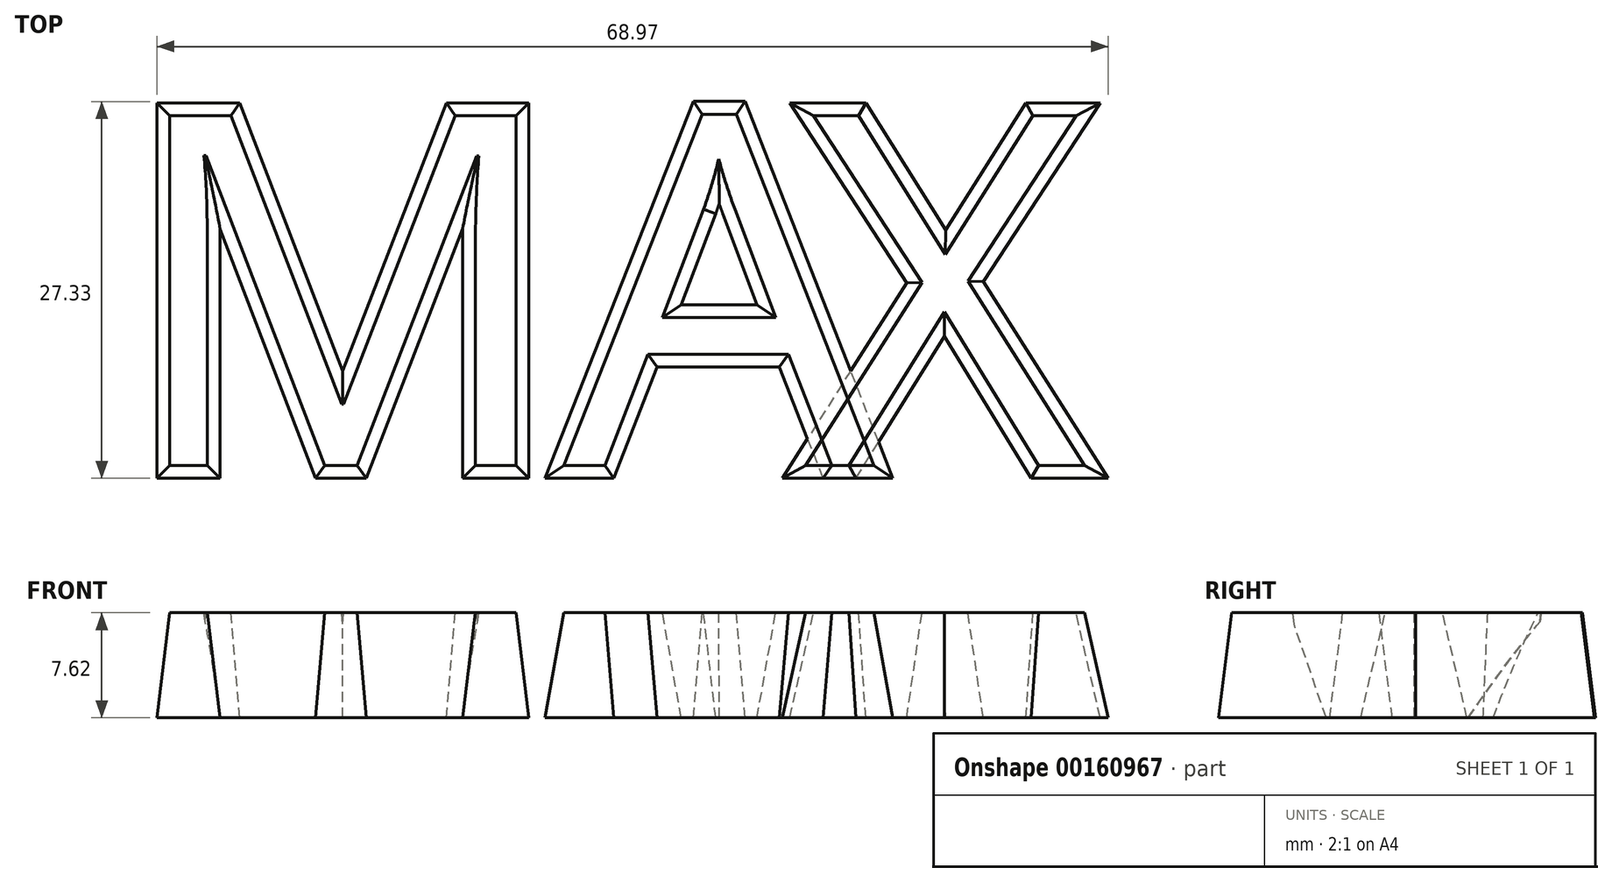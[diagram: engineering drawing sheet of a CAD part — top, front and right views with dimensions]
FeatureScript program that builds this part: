
annotation { "Feature Type Name" : "Feature", "Feature Type Description" : "" }
export const myFeature = defineFeature(function(context is Context, id is Id, definition is map)
    precondition{}
    {
        {
            var Q0;
            Q0=qCreatedBy(makeId("Top.planeOp"),FACE);
            var sketch = newSketch(context, id + "F0", { "sketchPlane" : qUnion([Q0])});
            skText(sketch, "E0", { "text": "MAX", "fontName": "OpenSans-Regular.ttf"});
            const initialGuessF0  = {"E0": [0.00322, 0, 1, 0, 0.02557]};
            skSetInitialGuess(sketch, initialGuessF0);
            skSolve(sketch);
        }
        {
            var Q0;
            Q0 = qSketchRegion(id + "F0", true);
            extrude(context, id + "F1", {"entities" : qUnion([Q0]), "oppositeDirection" : true, "depth" : 7.62 * mm, "hasDraft" : true, "draftAngle" : 7 * degree});
        }
        {
            var Q0;
            Q0=makeQuery(id+"F1.opExtrude","SWEPT_BODY",BODY,{"disambiguationData":[OSD([sQuery(id+"F0.wireOp",EDGE,"E0.sketch_text.stroke-31"),sQuery(id+"F0.wireOp",EDGE,"E0.sketch_text.stroke-32"),sQuery(id+"F0.wireOp",EDGE,"E0.sketch_text.stroke-33"),sQuery(id+"F0.wireOp",EDGE,"E0.sketch_text.stroke-34"),sQuery(id+"F0.wireOp",EDGE,"E0.sketch_text.stroke-35"),sQuery(id+"F0.wireOp",EDGE,"E0.sketch_text.stroke-36"),sQuery(id+"F0.wireOp",EDGE,"E0.sketch_text.stroke-37"),sQuery(id+"F0.wireOp",EDGE,"E0.sketch_text.stroke-38"),sQuery(id+"F0.wireOp",EDGE,"E0.sketch_text.stroke-39"),sQuery(id+"F0.wireOp",EDGE,"E0.sketch_text.stroke-40"),sQuery(id+"F0.wireOp",EDGE,"E0.sketch_text.stroke-41"),sQuery(id+"F0.wireOp",EDGE,"E0.sketch_text.stroke-42")])]});
            var Q1;
            Q1=makeQuery(id+"F1.opExtrude","CAP_EDGE",EDGE,{"disambiguationData":[OSD([sQuery(id+"F0.wireOp",EDGE,"E0.sketch_text.stroke-21")])],"isStart":false});
            transform(context, id + "F2", {"entities" : qUnion([Q0]), "transformType" : TransformType.TRANSLATION_DISTANCE, "transformDirection" : qUnion([Q1]), "distance" : 5.08 * mm, "makeCopy" : false});
        }
    });
